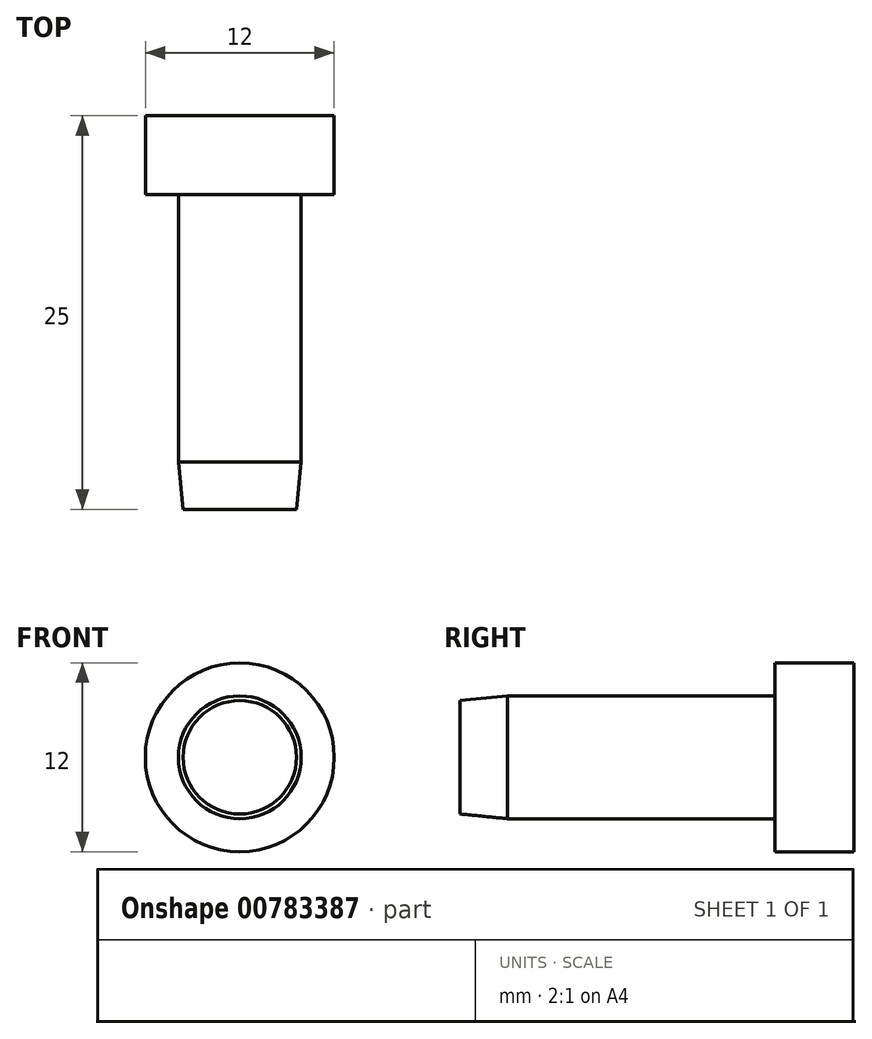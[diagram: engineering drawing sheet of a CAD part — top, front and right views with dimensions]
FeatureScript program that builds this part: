
annotation { "Feature Type Name" : "Feature", "Feature Type Description" : "" }
export const myFeature = defineFeature(function(context is Context, id is Id, definition is map)
    precondition{}
    {
        {
            var Q0;
            Q0=qCreatedBy(makeId("Front.planeOp"),FACE);
            var sketch = newSketch(context, id + "F0", { "sketchPlane" : qUnion([Q0])});
            skCircle(sketch, "E0", {"center": v(0, 0) * mm, "radius": 3.9 * mm});
            skCircle(sketch, "E1", {"center": v(0, 0) * mm, "radius": 6 * mm});
            skSolve(sketch);
        }
        {
            var Q0;
            Q0=makeQuery(id+"F0.imprint","IMPRINT",FACE,{"disambiguationData":[TD([[makeQuery(id+"F0.imprint","IMPRINT",EDGE,{"derivedFrom":sQuery(id+"F0.wireOp",EDGE,"E0")}),1.0]])]});
            extrude(context, id + "F1", {"entities" : qUnion([Q0]), "depth" : 25 * mm, "offsetDistance" : 25 * mm});
        }
        {
            var Q0;
            Q0=makeQuery(id+"F0.imprint","IMPRINT",FACE,{"disambiguationData":[TD([[makeQuery(id+"F0.imprint","IMPRINT",EDGE,{"derivedFrom":sQuery(id+"F0.wireOp",EDGE,"E0")}),-1.0]])]});
            extrude(context, id + "F2", {"entities" : qUnion([Q0]), "operationType" : NewBodyOperationType.ADD, "depth" : 5 * mm, "offsetDistance" : 25 * mm});
        }
        {
            var Q0;
            Q0=makeQuery(id+"F1.opExtrude","CAP_EDGE",EDGE,{"disambiguationData":[OSD([sQuery(id+"F0.wireOp",EDGE,"E0")])],"isStart":false});
            chamfer(context, id + "F3", {"entities" : qUnion([Q0]), "chamferType" : ChamferType.TWO_OFFSETS, "width1" : 0.3 * mm, "oppositeDirection" : false, "width2" : 3 * mm, "tangentPropagation" : true});
        }
    });
